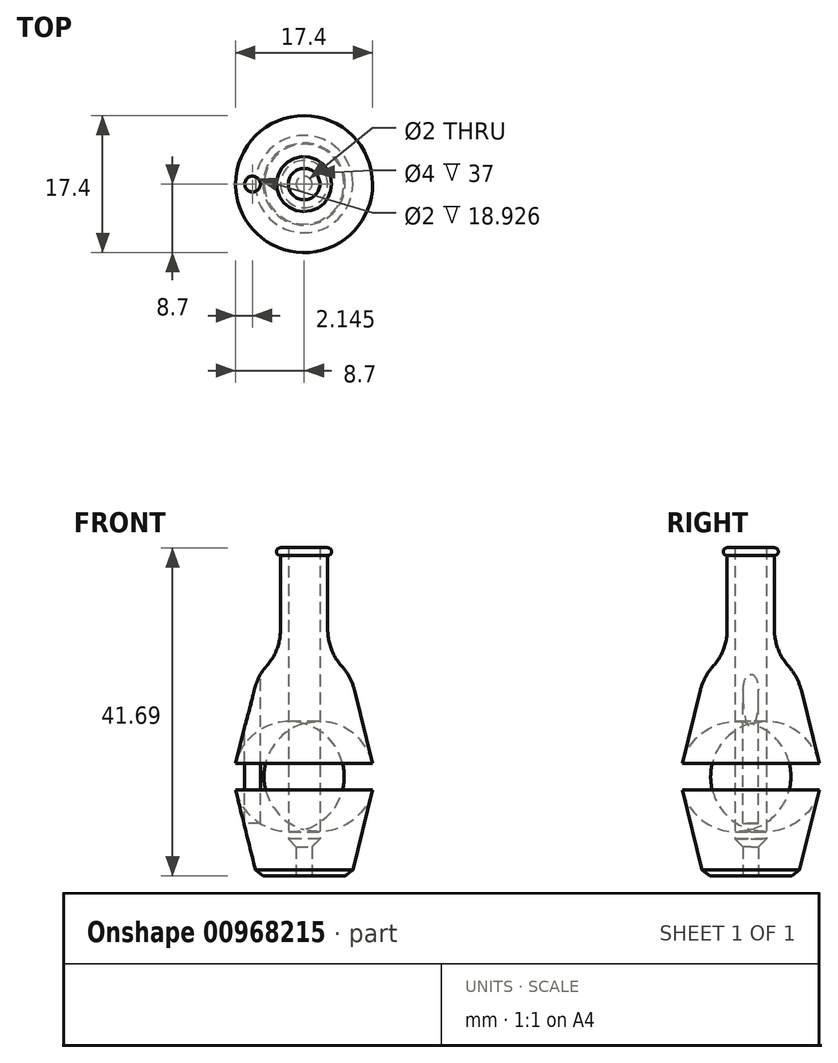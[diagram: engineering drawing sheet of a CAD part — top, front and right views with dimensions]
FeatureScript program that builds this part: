
annotation { "Feature Type Name" : "Feature", "Feature Type Description" : "" }
export const myFeature = defineFeature(function(context is Context, id is Id, definition is map)
    precondition{}
    {
        {
            var Q0;
            Q0=qCreatedBy(makeId("Front.planeOp"),FACE);
            var sketch = newSketch(context, id + "F0", { "sketchPlane" : qUnion([Q0])});
            skLineSegment(sketch, "E0", {"start": v(0, 0) * mm, "end": v(-6, 0) * mm});
            skLineSegment(sketch, "E1", {"start": v(-6, 0) * mm, "end": v(-9.11, 12.62) * mm});
            skLineSegment(sketch, "E2", {"start": v(-9.11, 12.62) * mm, "end": v(-6, 25.24) * mm});
            skLineSegment(sketch, "E3", {"start": v(-6, 25.24) * mm, "end": v(-3, 28.7) * mm});
            skLineSegment(sketch, "E4", {"start": v(-3, 28.7) * mm, "end": v(-3, 40.7) * mm});
            skLineSegment(sketch, "E5", {"start": v(-3, 40.7) * mm, "end": v(0, 40.7) * mm});
            skLineSegment(sketch, "E6", {"start": v(0, 40.7) * mm, "end": v(0, 0) * mm, "construction": true});
            skLineSegment(sketch, "E7", {"start": v(0, 40.7) * mm, "end": v(0, 0) * mm});
            skSolve(sketch);
        }
        {
            var Q0;
            Q0=makeQuery(id+"F0.imprint","IMPRINT",FACE,{"disambiguationData":[TD([[makeQuery(id+"F0.imprint","IMPRINT",EDGE,{"derivedFrom":sQuery(id+"F0.wireOp",EDGE,"E0")}),-1.0]])]});
            var Q1;
            Q1=sQuery(id+"F0.wireOp",EDGE,"E7");
            revolve(context, id + "F1", {"surfaceOperationType" : NewSurfaceOperationType.NEW, "entities" : qUnion([Q0]), "axis" : qUnion([Q1]), "revolveType" : RevolveType.FULL});
        }
        {
            var Q0;
            Q0=qCreatedBy(makeId("Top.planeOp"),FACE);
            var sketch = newSketch(context, id + "F2", { "sketchPlane" : qUnion([Q0])});
            skCircle(sketch, "E8", {"center": v(0, 0) * mm, "radius": 1 * mm});
            skSolve(sketch);
        }
        {
            var Q0;
            Q0=makeQuery(id+"F2.imprint","IMPRINT",FACE,{"disambiguationData":[TD([[makeQuery(id+"F2.imprint","IMPRINT",EDGE,{"derivedFrom":sQuery(id+"F2.wireOp",EDGE,"E8")}),1.0]])]});
            extrude(context, id + "F3", {"entities" : qUnion([Q0]), "operationType" : NewBodyOperationType.REMOVE, "oppositeDirection" : true, "depth" : -10 * mm, "offsetDistance" : 25 * mm});
        }
        {
            var Q0;
            Q0=makeQuery(id+"F1.opRevolve","SWEPT_FACE",FACE,{"disambiguationData":[OSD([sQuery(id+"F0.wireOp",EDGE,"E5")])]});
            var sketch = newSketch(context, id + "F4", { "sketchPlane" : qUnion([Q0])});
            skCircle(sketch, "E9", {"center": v(0, 0) * mm, "radius": 2 * mm});
            skCircle(sketch, "E10", {"center": v(0, 0) * mm, "radius": 3.5 * mm});
            skSolve(sketch);
        }
        {
            var Q0;
            Q0 = qSketchRegion(id + "F4", true);
            extrude(context, id + "F5", {"entities" : qUnion([Q0]), "operationType" : NewBodyOperationType.ADD, "depth" : 1 * mm, "offsetDistance" : 25 * mm});
        }
        {
            var Q0;
            Q0=makeQuery(id+"F1.opRevolve","SWEPT_FACE",FACE,{"disambiguationData":[OSD([sQuery(id+"F0.wireOp",EDGE,"E5")])]});
            extrude(context, id + "F6", {"entities" : qUnion([Q0]), "operationType" : NewBodyOperationType.REMOVE, "oppositeDirection" : true, "depth" : 35 * mm, "offsetDistance" : 25 * mm});
        }
        {
            var Q0;
            Q0=makeQuery(id+"F6.boolean.opBoolean","INTERSECT",EDGE,{"derivedFrom":[makeQuery(id+"F3.boolean.opBoolean","COPY",FACE,{"derivedFrom":makeQuery(id+"F3.opExtrude","SWEPT_FACE",FACE,{"disambiguationData":[OSD([sQuery(id+"F2.wireOp",EDGE,"E8")])]})}),makeQuery(id+"F6.opExtrude","CAP_FACE",FACE,{"disambiguationData":[OSD([sQuery(id+"F0.wireOp",EDGE,"E5")])],"isStart":false})]});
            chamfer(context, id + "F7", {"entities" : qUnion([Q0]), "width" : 2 * mm, "tangentPropagation" : true});
        }
        {
            var Q0;
            Q0=makeQuery(id+"F5.opExtrude","CAP_EDGE",EDGE,{"disambiguationData":[OSD([sQuery(id+"F4.wireOp",EDGE,"E10")])],"isStart":false});
            var Q1;
            Q1=makeQuery(id+"F5.opExtrude","CAP_EDGE",EDGE,{"disambiguationData":[OSD([sQuery(id+"F4.wireOp",EDGE,"E10")])],"isStart":true});
            fillet(context, id + "F8", {"entities" : qUnion([Q0, Q1]), "radius" : .5 * mm, "tangentPropagation" : true, "allowEdgeOverflow" : false});
        }
        {
            var Q0;
            Q0=makeQuery(id+"F1.opRevolve","SWEPT_EDGE",EDGE,{"disambiguationData":[OSD([sQuery(id+"F0.wireOp",EDGE,"E3"),sQuery(id+"F0.wireOp",EDGE,"E4")])]});
            var Q1;
            Q1=makeQuery(id+"F1.opRevolve","SWEPT_EDGE",EDGE,{"disambiguationData":[OSD([sQuery(id+"F0.wireOp",EDGE,"E2"),sQuery(id+"F0.wireOp",EDGE,"E3")])]});
            var Q2;
            Q2=makeQuery(id+"F1.opRevolve","SWEPT_EDGE",EDGE,{"disambiguationData":[OSD([sQuery(id+"F0.wireOp",EDGE,"E1"),sQuery(id+"F0.wireOp",EDGE,"E2")])]});
            fillet(context, id + "F9", {"entities" : qUnion([Q0, Q1, Q2]), "radius" : 7 * mm, "tangentPropagation" : true, "allowEdgeOverflow" : false});
        }
        {
            var Q0;
            Q0=makeQuery(id+"F1.opRevolve","SWEPT_EDGE",EDGE,{"disambiguationData":[OSD([sQuery(id+"F0.wireOp",EDGE,"E0"),sQuery(id+"F0.wireOp",EDGE,"E1")])]});
            chamfer(context, id + "F10", {"entities" : qUnion([Q0]), "width" : 1 * mm, "tangentPropagation" : true});
        }
        {
            var Q0;
            Q0=makeQuery(id+"F5.opExtrude","CAP_FACE",FACE,{"disambiguationData":[OSD([sQuery(id+"F4.wireOp",EDGE,"E9"),sQuery(id+"F4.wireOp",EDGE,"E10")])],"isStart":false});
            var sketch = newSketch(context, id + "F11", { "sketchPlane" : qUnion([Q0])});
            skCircle(sketch, "E11", {"center": v(-6.55, 0) * mm, "radius": 1 * mm});
            skSolve(sketch);
        }
        {
            var Q0;
            Q0=makeQuery(id+"F11.imprint","IMPRINT",FACE,{"disambiguationData":[TD([[makeQuery(id+"F11.imprint","IMPRINT",EDGE,{"derivedFrom":sQuery(id+"F11.wireOp",EDGE,"E11")}),1.0]])]});
            extrude(context, id + "F12", {"entities" : qUnion([Q0]), "operationType" : NewBodyOperationType.REMOVE, "oppositeDirection" : true, "depth" : 35 * mm, "offsetDistance" : 25 * mm});
        }
    });
